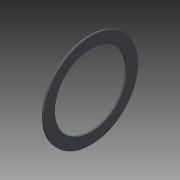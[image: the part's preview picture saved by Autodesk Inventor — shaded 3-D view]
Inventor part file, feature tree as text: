
AUTODESK INVENTOR PART (.ipt)
format: ipt  version: 2014 SP2 (Build 180246200, 246)  size: 95,744 bytes
history: native  units: mm
features: other x7, revolve x1, sketch x1
ambient origin geometry x8: Origin, YZ Plane, XZ Plane, XY Plane, X Axis, Y Axis, Z Axis, Center Point
bodies: Solid1 (feature_tree)
feature tree (9):
  revolve  "Revolution1"  [1 undecoded]
  other  "ip_st_1_XY"
  other  "ip_st_1_YZ"
  other  "ip_st_1_ZX"
  other  "ip_st_1_X"
  other  "ip_st_1_Y"
  other  "ip_st_1_Z"
  other  "ip_st_1_Center"
  sketch  "Sketch_1"  dims[d0=360.0deg d1=0.0mm]
note: 1 required parameter value undecoded (feature->parameter linkage not recoverable at this tier; creation-order binding heuristic only, values carry confidence <= 0.55)
